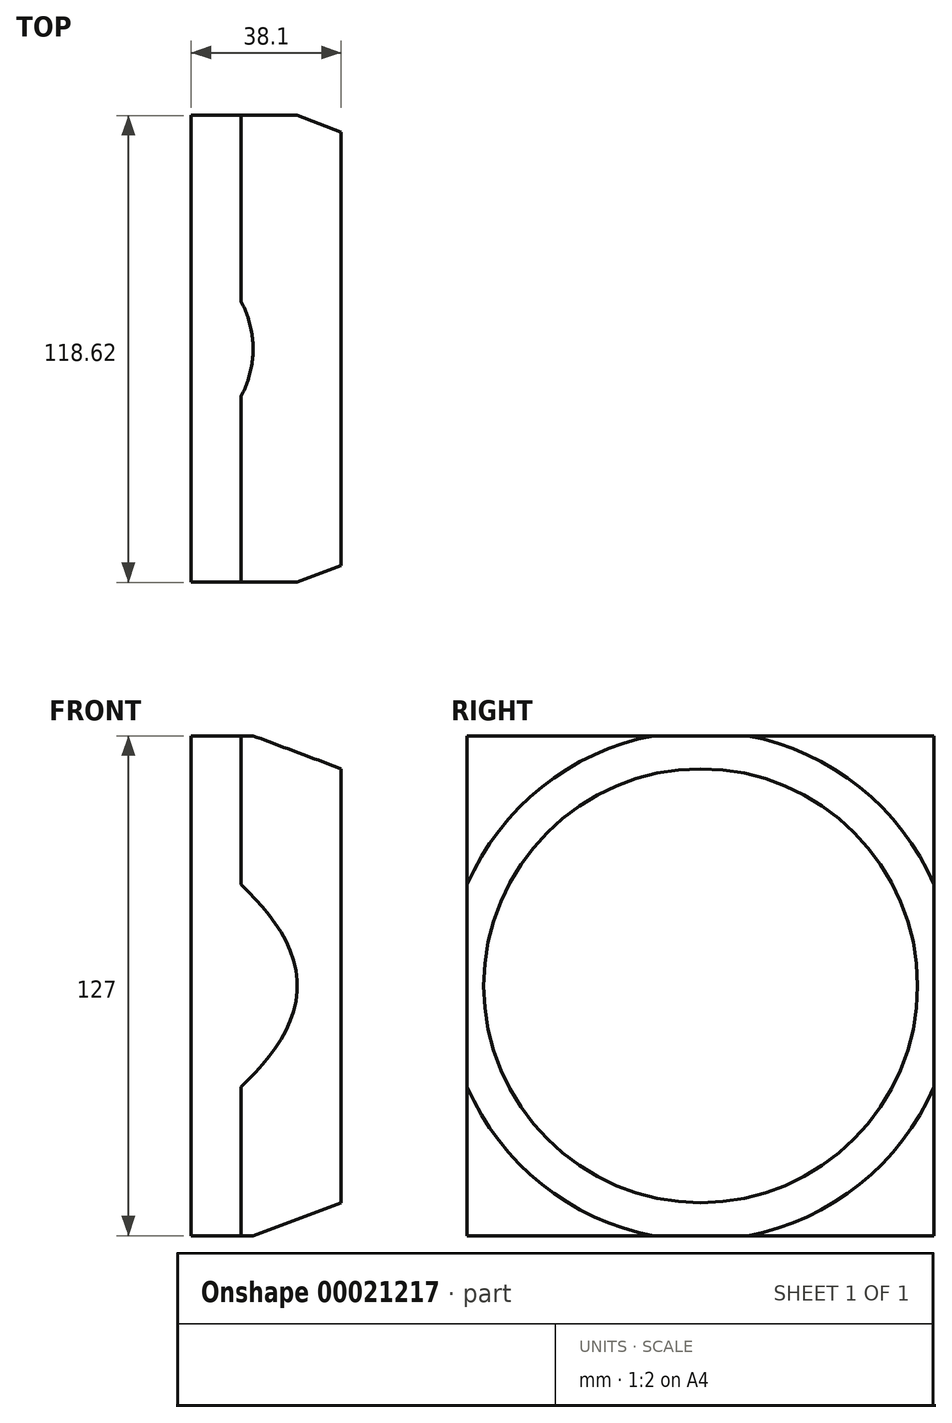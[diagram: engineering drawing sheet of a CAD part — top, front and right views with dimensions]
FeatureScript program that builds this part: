
annotation { "Feature Type Name" : "Feature", "Feature Type Description" : "" }
export const myFeature = defineFeature(function(context is Context, id is Id, definition is map)
    precondition{}
    {
        {
            var Q0;
            Q0=qCreatedBy(makeId("Right.planeOp"),FACE);
            var sketch = newSketch(context, id + "F0", { "sketchPlane" : qUnion([Q0])});
            skLineSegment(sketch, "E0.bottom", {"start": v(-60.93, 79.23) * mm, "end": v(57.7, 79.23) * mm});
            skLineSegment(sketch, "E0.top", {"start": v(-60.93, -47.77) * mm, "end": v(57.7, -47.77) * mm});
            skLineSegment(sketch, "E0.left", {"start": v(-60.93, 79.23) * mm, "end": v(-60.93, -47.77) * mm});
            skLineSegment(sketch, "E0.right", {"start": v(57.7, 79.23) * mm, "end": v(57.7, -47.77) * mm});
            skSolve(sketch);
        }
        {
            var Q0;
            Q0=makeQuery(id+"F0.imprint","IMPRINT",FACE,{"disambiguationData":[TD([[makeQuery(id+"F0.imprint","IMPRINT",EDGE,{"derivedFrom":sQuery(id+"F0.wireOp",EDGE,"E0.bottom")}),-1.0]])]});
            extrude(context, id + "F1", {"entities" : qUnion([Q0]), "depth" : 38.1 * mm});
        }
        {
            var Q0;
            Q0=makeQuery(id+"F1.opExtrude","CAP_EDGE",EDGE,{"disambiguationData":[OSD([sQuery(id+"F0.wireOp",EDGE,"E0.bottom")])],"isStart":false});
            cPlane(context, id + "F2", {"entities" : qUnion([Q0]), "cplaneType" : CPlaneType.MID_PLANE, "offset" : 152.4 * mm, "width" : 152.4 * mm, "height" : 152.4 * mm});
        }
        {
            var Q0;
            Q0=qCreatedBy(id+"F2.planeOp",FACE);
            var sketch = newSketch(context, id + "F3", { "sketchPlane" : qUnion([Q0])});
            skLineSegment(sketch, "E1", {"start": v(-995.2, 15.73) * mm, "end": v(540.03, 15.73) * mm, "construction": true});
            skLineSegment(sketch, "E2", {"start": v(-38.1, 104.63) * mm, "end": v(-38.1, 70.84) * mm});
            skLineSegment(sketch, "E3", {"start": v(-12.7, 104.63) * mm, "end": v(-38.1, 104.63) * mm});
            skLineSegment(sketch, "E4", {"start": v(-38.1, 70.84) * mm, "end": v(-12.7, 80.35) * mm});
            skLineSegment(sketch, "E5", {"start": v(-12.7, 80.35) * mm, "end": v(-12.7, 104.63) * mm});
            skSolve(sketch);
        }
        {
            var Q0;
            Q0=makeQuery(id+"F3.imprint","IMPRINT",FACE,{"disambiguationData":[TD([[makeQuery(id+"F3.imprint","IMPRINT",EDGE,{"derivedFrom":sQuery(id+"F3.wireOp",EDGE,"E2")}),1.0]])]});
            var Q1;
            Q1=sQuery(id+"F3.wireOp",EDGE,"c68b134b-dae5-49d7-870c-037785c0a059");
            var Q2;
            Q2=sQuery(id+"F3.wireOp",EDGE,"E2");
            var Q3;
            Q3=sQuery(id+"F3.wireOp",EDGE,"E3");
            var Q4;
            Q4=sQuery(id+"F3.wireOp",EDGE,"E1");
            revolve(context, id + "F4", {"operationType" : NewBodyOperationType.REMOVE, "entities" : qUnion([Q0]), "surfaceEntities" : qUnion([Q1, Q2, Q3]), "axis" : qUnion([Q4]), "revolveType" : RevolveType.FULL, "oppositeDirection" : true});
        }
    });
